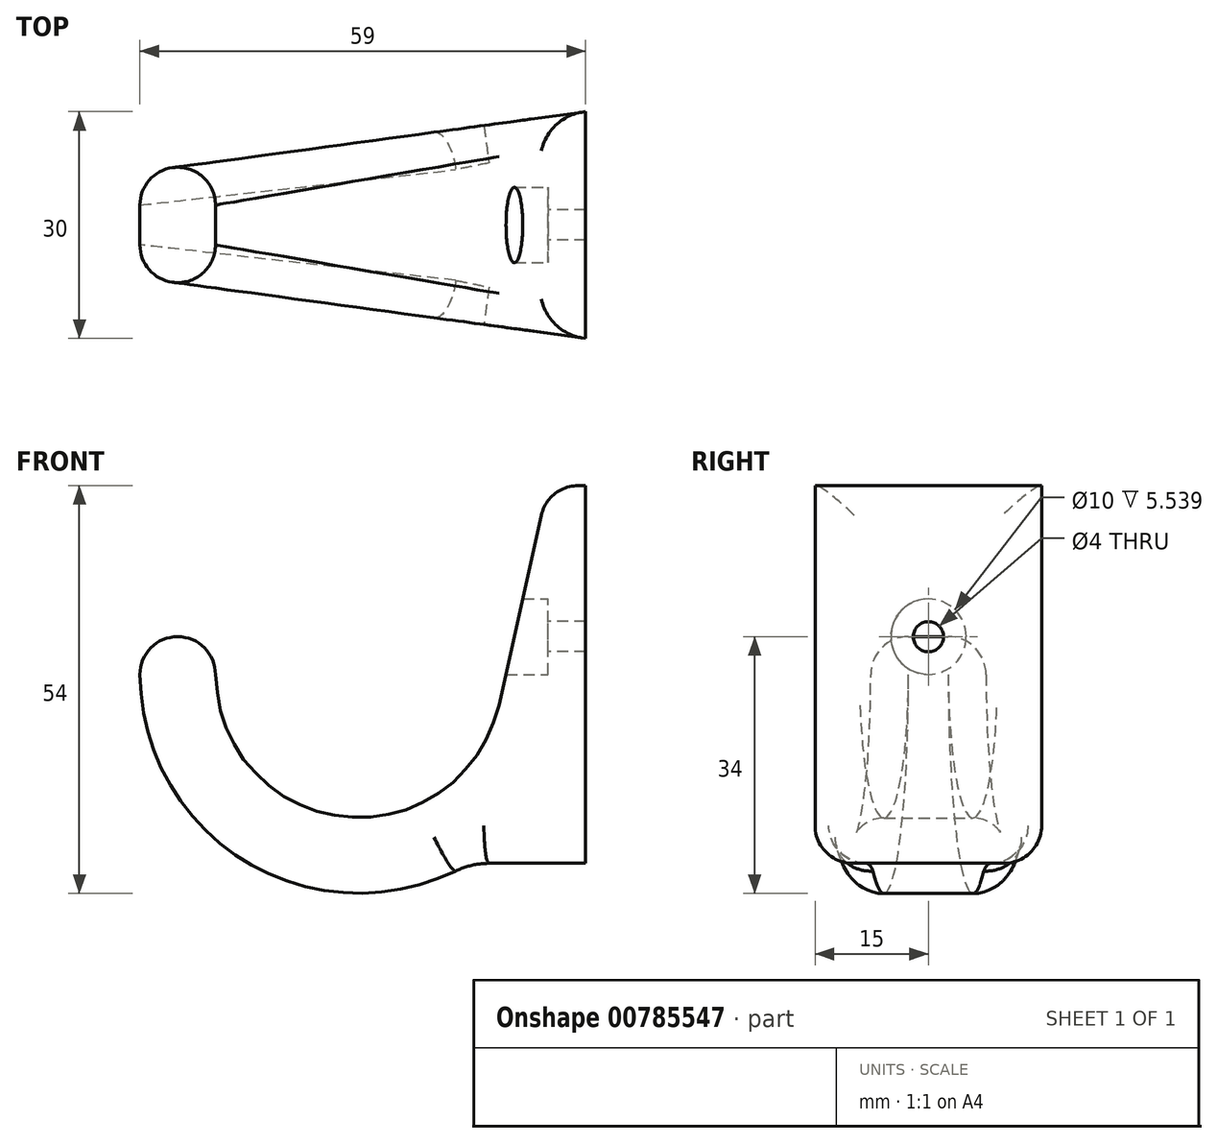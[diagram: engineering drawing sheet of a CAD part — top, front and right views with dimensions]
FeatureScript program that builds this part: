
annotation { "Feature Type Name" : "Feature", "Feature Type Description" : "" }
export const myFeature = defineFeature(function(context is Context, id is Id, definition is map)
    precondition{}
    {
        {
            var Q0;
            Q0=qCreatedBy(makeId("Front.planeOp"),FACE);
            var sketch = newSketch(context, id + "F0", { "sketchPlane" : qUnion([Q0])});
            skLineSegment(sketch, "E0", {"start": v(0, -50) * mm, "end": v(0, 0) * mm});
            skLineSegment(sketch, "E1", {"start": v(0, 0) * mm, "end": v(-5, 0) * mm});
            skLineSegment(sketch, "E2", {"start": v(-12.8, -50) * mm, "end": v(0, -50) * mm});
            skLineSegment(sketch, "E3", {"start": v(-5, 0) * mm, "end": v(-11.45, -29.11) * mm});
            skArc(sketch, "E4", {"start": v(-49, -25) * mm, "mid": v(-32.07, -43.89) * mm, "end": v(-11.45, -29.11) * mm});
            skArc(sketch, "E5", {"start": v(-59, -25) * mm, "mid": v(-45.33, -49.62) * mm, "end": v(-17.2, -51.03) * mm});
            skArc(sketch, "E6", {"start": v(-49, -25) * mm, "mid": v(-54, -20) * mm, "end": v(-59, -25) * mm});
            skPoint(sketch, "E7.visualSharp", {"position": v(-15.3, -50) * mm});
            skArc(sketch, "E7.filletArc", {"start": v(-12.8, -50) * mm, "mid": v(-15.06, -50.26) * mm, "end": v(-17.2, -51.03) * mm});
            skLineSegment(sketch, "E8", {"start": v(-54, -25) * mm, "end": v(-30, -25) * mm, "construction": true});
            skSolve(sketch);
        }
        {
            var Q0;
            Q0 = qSketchRegion(id + "F0", true);
            extrude(context, id + "F1", {"entities" : qUnion([Q0]), "depth" : 15 * mm, "offsetDistance" : 25 * mm});
        }
        {
            var Q0;
            Q0=qCreatedBy(makeId("Top.planeOp"),FACE);
            var sketch = newSketch(context, id + "F2", { "sketchPlane" : qUnion([Q0])});
            skLineSegment(sketch, "E9.top", {"start": v(-59, -40) * mm, "end": v(0, -40) * mm});
            skLineSegment(sketch, "E9.left", {"start": v(-59, -7) * mm, "end": v(-59, -40) * mm});
            skLineSegment(sketch, "E9.right", {"start": v(0, -15) * mm, "end": v(0, -40) * mm});
            skLineSegment(sketch, "E10", {"start": v(-59, -7) * mm, "end": v(0, -15) * mm});
            skSolve(sketch);
        }
        {
            var Q0;
            Q0 = qSketchRegion(id + "F2", true);
            extrude(context, id + "F3", {"entities" : qUnion([Q0]), "operationType" : NewBodyOperationType.REMOVE, "endBound" : BoundingType.THROUGH_ALL, "oppositeDirection" : true, "depth" : 25 * mm, "offsetDistance" : 25 * mm});
        }
        {
            var Q0;
            Q0=makeQuery(id+"F1.opExtrude","SWEPT_BODY",BODY,{"disambiguationData":[OSD([sQuery(id+"F0.wireOp",EDGE,"E0"),sQuery(id+"F0.wireOp",EDGE,"E1"),sQuery(id+"F0.wireOp",EDGE,"E2"),sQuery(id+"F0.wireOp",EDGE,"E3"),sQuery(id+"F0.wireOp",EDGE,"E4"),sQuery(id+"F0.wireOp",EDGE,"E5"),sQuery(id+"F0.wireOp",EDGE,"E6"),sQuery(id+"F0.wireOp",EDGE,"E7.filletArc")])]});
            var Q1;
            Q1=qCreatedBy(makeId("Front.planeOp"),FACE);
            mirror(context, id + "F4", {"operationType" : NewBodyOperationType.ADD, "entities" : qUnion([Q0]), "mirrorPlane" : qUnion([Q1])});
        }
        {
            var Q0;
            Q0=makeQuery(id+"F4.opPattern","COPY",EDGE,{"derivedFrom":makeQuery(id+"F3.boolean.opBoolean","INTERSECT",EDGE,{"derivedFrom":[makeQuery(id+"F1.opExtrude","SWEPT_FACE",FACE,{"disambiguationData":[OSD([sQuery(id+"F0.wireOp",EDGE,"E5")])]}),makeQuery(id+"F3.opExtrude","SWEPT_FACE",FACE,{"disambiguationData":[OSD([sQuery(id+"F2.wireOp",EDGE,"E10")])]})]}),"instanceName":"1"});
            var Q1;
            Q1=makeQuery(id+"F3.boolean.opBoolean","INTERSECT",EDGE,{"derivedFrom":[makeQuery(id+"F1.opExtrude","SWEPT_FACE",FACE,{"disambiguationData":[OSD([sQuery(id+"F0.wireOp",EDGE,"E4")])]}),makeQuery(id+"F3.opExtrude","SWEPT_FACE",FACE,{"disambiguationData":[OSD([sQuery(id+"F2.wireOp",EDGE,"E10")])]})]});
            var Q2;
            {var subQ0=makeQuery(id+"F1.opExtrude","SWEPT_EDGE",EDGE,{"disambiguationData":[OSD([sQuery(id+"F0.wireOp",EDGE,"E1"),sQuery(id+"F0.wireOp",EDGE,"E3")])]});Q2=makeQuery(id+"F4.boolean.opBoolean","MERGE",EDGE,{"derivedFrom":[subQ0,makeQuery(id+"F4.opPattern","COPY",EDGE,{"derivedFrom":subQ0,"instanceName":"1"})]});}
            fillet(context, id + "F5", {"entities" : qUnion([Q0, Q1, Q2]), "radius" : 5 * mm, "tangentPropagation" : true, "allowEdgeOverflow" : false});
        }
        {
            var Q0;
            Q0=qCreatedBy(makeId("Right.planeOp"),FACE);
            cPlane(context, id + "F6", {"entities" : qUnion([Q0]), "cplaneType" : CPlaneType.OFFSET, "offset" : 5 * mm, "oppositeDirection" : true, "width" : 150 * mm, "height" : 150 * mm});
        }
        {
            var Q0;
            Q0=qCreatedBy(id+"F6.planeOp",FACE);
            var sketch = newSketch(context, id + "F7", { "sketchPlane" : qUnion([Q0])});
            skCircle(sketch, "E11", {"center": v(0, -20) * mm, "radius": 5 * mm});
            skSolve(sketch);
        }
        {
            var Q0;
            Q0 = qSketchRegion(id + "F7", true);
            extrude(context, id + "F8", {"entities" : qUnion([Q0]), "operationType" : NewBodyOperationType.REMOVE, "endBound" : BoundingType.UP_TO_NEXT, "oppositeDirection" : true, "depth" : 25 * mm, "offsetDistance" : 25 * mm});
        }
        {
            var Q0;
            Q0=qCreatedBy(id+"F6.planeOp",FACE);
            var sketch = newSketch(context, id + "F9", { "sketchPlane" : qUnion([Q0])});
            skCircle(sketch, "E12", {"center": v(0, -20) * mm, "radius": 2 * mm});
            skSolve(sketch);
        }
        {
            var Q0;
            Q0 = qSketchRegion(id + "F9", true);
            extrude(context, id + "F10", {"entities" : qUnion([Q0]), "operationType" : NewBodyOperationType.REMOVE, "endBound" : BoundingType.UP_TO_NEXT, "depth" : 25 * mm, "offsetDistance" : 25 * mm});
        }
    });
